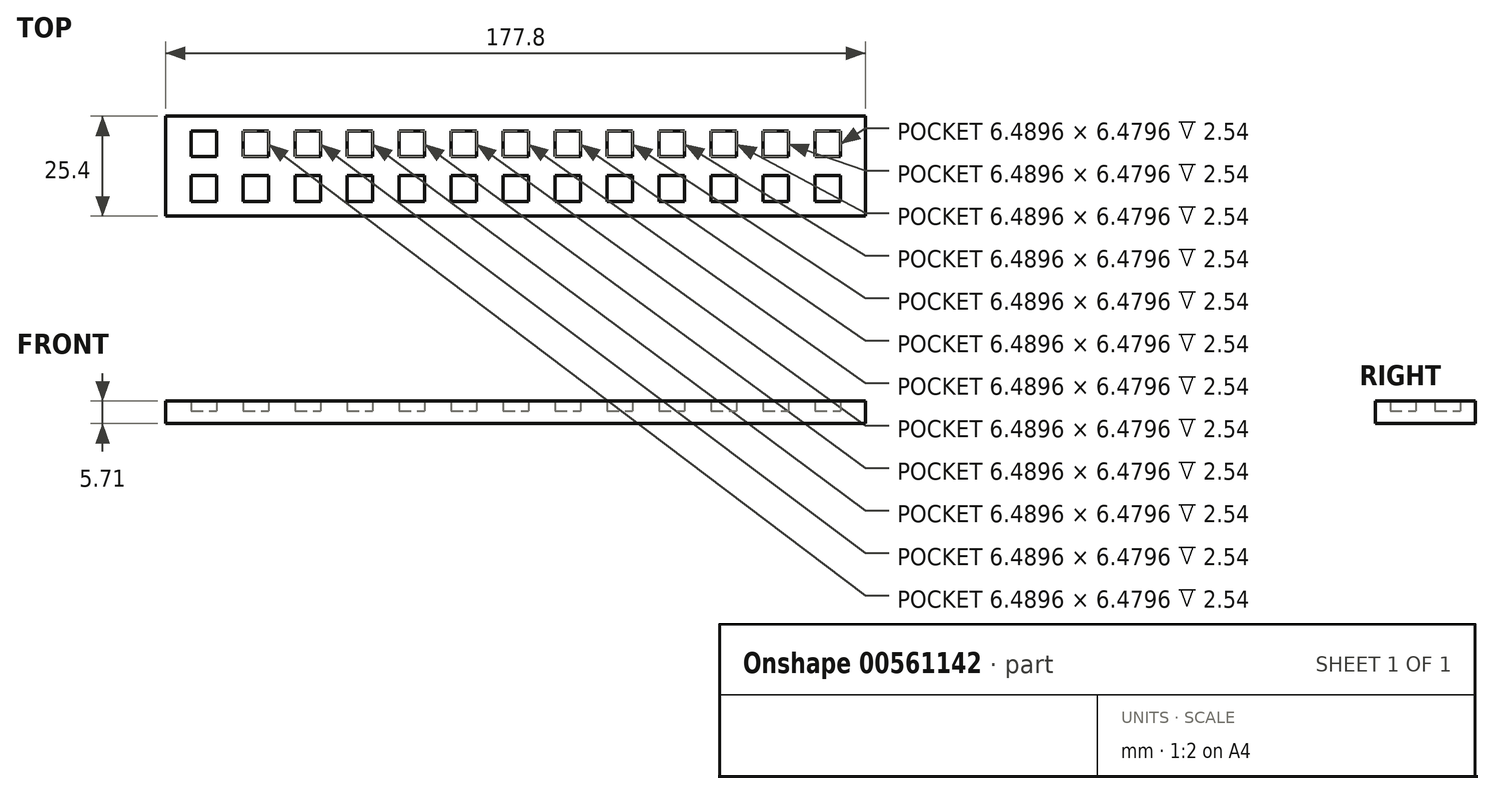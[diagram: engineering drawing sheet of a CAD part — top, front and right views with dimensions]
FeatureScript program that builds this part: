
annotation { "Feature Type Name" : "Feature", "Feature Type Description" : "" }
export const myFeature = defineFeature(function(context is Context, id is Id, definition is map)
    precondition{}
    {
        {
            var Q0;
            Q0=qCreatedBy(makeId("Top.planeOp"),FACE);
            var sketch = newSketch(context, id + "F0", { "sketchPlane" : qUnion([Q0])});
            skLineSegment(sketch, "E0.bottom", {"start": v(0, 0) * mm, "end": v(177.8, 0) * mm});
            skLineSegment(sketch, "E0.top", {"start": v(0, 25.4) * mm, "end": v(177.8, 25.4) * mm});
            skLineSegment(sketch, "E0.left", {"start": v(0, 0) * mm, "end": v(0, 25.4) * mm});
            skLineSegment(sketch, "E0.right", {"start": v(177.8, 0) * mm, "end": v(177.8, 25.4) * mm});
            skSolve(sketch);
        }
        {
            var Q0;
            Q0=makeQuery(id+"F0.imprint","IMPRINT",FACE,{"disambiguationData":[TD([[makeQuery(id+"F0.imprint","IMPRINT",EDGE,{"derivedFrom":sQuery(id+"F0.wireOp",EDGE,"E0.bottom")}),1.0]])]});
            extrude(context, id + "F1", {"entities" : qUnion([Q0]), "depth" : 3.17 * mm, "offsetDistance" : 25.4 * mm});
        }
        {
            var Q0;
            Q0=makeQuery(id+"F1.opExtrude","CAP_FACE",FACE,{"disambiguationData":[OSD([sQuery(id+"F0.wireOp",EDGE,"E0.bottom"),sQuery(id+"F0.wireOp",EDGE,"E0.top"),sQuery(id+"F0.wireOp",EDGE,"E0.left"),sQuery(id+"F0.wireOp",EDGE,"E0.right")])],"isStart":false});
            var sketch = newSketch(context, id + "F2", { "sketchPlane" : qUnion([Q0])});
            skLineSegment(sketch, "E1.right", {"start": v(6.49, 15.11) * mm, "end": v(6.49, 21.6) * mm});
            skLineSegment(sketch, "E2.bottom", {"start": v(6.49, 15.11) * mm, "end": v(12.98, 15.11) * mm});
            skLineSegment(sketch, "E2.top", {"start": v(6.49, 21.6) * mm, "end": v(12.98, 21.6) * mm});
            skLineSegment(sketch, "E2.right", {"start": v(12.98, 15.11) * mm, "end": v(12.98, 21.6) * mm});
            skLineSegment(sketch, "E3.1.0.0", {"start": v(19.7, 21.6) * mm, "end": v(26.19, 21.6) * mm});
            skLineSegment(sketch, "E3.1.0.1", {"start": v(19.7, 15.11) * mm, "end": v(19.7, 21.6) * mm});
            skLineSegment(sketch, "E3.1.0.2", {"start": v(19.7, 15.11) * mm, "end": v(26.19, 15.11) * mm});
            skLineSegment(sketch, "E3.1.0.3", {"start": v(26.19, 15.11) * mm, "end": v(26.19, 21.6) * mm});
            skLineSegment(sketch, "E3.2.0.0", {"start": v(32.9, 21.6) * mm, "end": v(39.4, 21.6) * mm});
            skLineSegment(sketch, "E3.2.0.1", {"start": v(32.9, 15.11) * mm, "end": v(32.9, 21.6) * mm});
            skLineSegment(sketch, "E3.2.0.2", {"start": v(32.9, 15.11) * mm, "end": v(39.4, 15.11) * mm});
            skLineSegment(sketch, "E3.2.0.3", {"start": v(39.4, 15.11) * mm, "end": v(39.4, 21.6) * mm});
            skLineSegment(sketch, "E3.3.0.0", {"start": v(46.11, 21.6) * mm, "end": v(52.6, 21.6) * mm});
            skLineSegment(sketch, "E3.3.0.1", {"start": v(46.11, 15.11) * mm, "end": v(46.11, 21.6) * mm});
            skLineSegment(sketch, "E3.3.0.2", {"start": v(46.11, 15.11) * mm, "end": v(52.6, 15.11) * mm});
            skLineSegment(sketch, "E3.3.0.3", {"start": v(52.6, 15.11) * mm, "end": v(52.6, 21.6) * mm});
            skLineSegment(sketch, "E3.4.0.0", {"start": v(59.32, 21.6) * mm, "end": v(65.81, 21.6) * mm});
            skLineSegment(sketch, "E3.4.0.1", {"start": v(59.32, 15.11) * mm, "end": v(59.32, 21.6) * mm});
            skLineSegment(sketch, "E3.4.0.2", {"start": v(59.32, 15.11) * mm, "end": v(65.81, 15.11) * mm});
            skLineSegment(sketch, "E3.4.0.3", {"start": v(65.81, 15.11) * mm, "end": v(65.81, 21.6) * mm});
            skLineSegment(sketch, "E3.5.0.0", {"start": v(72.53, 21.6) * mm, "end": v(79.02, 21.6) * mm});
            skLineSegment(sketch, "E3.5.0.1", {"start": v(72.53, 15.11) * mm, "end": v(72.53, 21.6) * mm});
            skLineSegment(sketch, "E3.5.0.2", {"start": v(72.53, 15.11) * mm, "end": v(79.02, 15.11) * mm});
            skLineSegment(sketch, "E3.5.0.3", {"start": v(79.02, 15.11) * mm, "end": v(79.02, 21.6) * mm});
            skLineSegment(sketch, "E3.6.0.0", {"start": v(85.74, 21.6) * mm, "end": v(92.23, 21.6) * mm});
            skLineSegment(sketch, "E3.6.0.1", {"start": v(85.74, 15.11) * mm, "end": v(85.74, 21.6) * mm});
            skLineSegment(sketch, "E3.6.0.2", {"start": v(85.74, 15.11) * mm, "end": v(92.23, 15.11) * mm});
            skLineSegment(sketch, "E3.6.0.3", {"start": v(92.23, 15.11) * mm, "end": v(92.23, 21.6) * mm});
            skLineSegment(sketch, "E3.7.0.0", {"start": v(98.95, 21.6) * mm, "end": v(105.44, 21.6) * mm});
            skLineSegment(sketch, "E3.7.0.1", {"start": v(98.95, 15.11) * mm, "end": v(98.95, 21.6) * mm});
            skLineSegment(sketch, "E3.7.0.2", {"start": v(98.95, 15.11) * mm, "end": v(105.44, 15.11) * mm});
            skLineSegment(sketch, "E3.7.0.3", {"start": v(105.44, 15.11) * mm, "end": v(105.44, 21.6) * mm});
            skLineSegment(sketch, "E3.8.0.0", {"start": v(112.15, 21.6) * mm, "end": v(118.64, 21.6) * mm});
            skLineSegment(sketch, "E3.8.0.1", {"start": v(112.15, 15.11) * mm, "end": v(112.15, 21.6) * mm});
            skLineSegment(sketch, "E3.8.0.2", {"start": v(112.15, 15.11) * mm, "end": v(118.64, 15.11) * mm});
            skLineSegment(sketch, "E3.8.0.3", {"start": v(118.64, 15.11) * mm, "end": v(118.64, 21.6) * mm});
            skLineSegment(sketch, "E3.9.0.0", {"start": v(125.36, 21.6) * mm, "end": v(131.85, 21.6) * mm});
            skLineSegment(sketch, "E3.9.0.1", {"start": v(125.36, 15.11) * mm, "end": v(125.36, 21.6) * mm});
            skLineSegment(sketch, "E3.9.0.2", {"start": v(125.36, 15.11) * mm, "end": v(131.85, 15.11) * mm});
            skLineSegment(sketch, "E3.9.0.3", {"start": v(131.85, 15.11) * mm, "end": v(131.85, 21.6) * mm});
            skLineSegment(sketch, "E3.10.0.0", {"start": v(138.57, 21.6) * mm, "end": v(145.06, 21.6) * mm});
            skLineSegment(sketch, "E3.10.0.1", {"start": v(138.57, 15.11) * mm, "end": v(138.57, 21.6) * mm});
            skLineSegment(sketch, "E3.10.0.2", {"start": v(138.57, 15.11) * mm, "end": v(145.06, 15.11) * mm});
            skLineSegment(sketch, "E3.10.0.3", {"start": v(145.06, 15.11) * mm, "end": v(145.06, 21.6) * mm});
            skLineSegment(sketch, "E3.11.0.0", {"start": v(151.78, 21.6) * mm, "end": v(158.27, 21.6) * mm});
            skLineSegment(sketch, "E3.11.0.1", {"start": v(151.78, 15.11) * mm, "end": v(151.78, 21.6) * mm});
            skLineSegment(sketch, "E3.11.0.2", {"start": v(151.78, 15.11) * mm, "end": v(158.27, 15.11) * mm});
            skLineSegment(sketch, "E3.11.0.3", {"start": v(158.27, 15.11) * mm, "end": v(158.27, 21.6) * mm});
            skLineSegment(sketch, "E3.12.0.0", {"start": v(164.99, 21.6) * mm, "end": v(171.48, 21.6) * mm});
            skLineSegment(sketch, "E3.12.0.1", {"start": v(164.99, 15.11) * mm, "end": v(164.99, 21.6) * mm});
            skLineSegment(sketch, "E3.12.0.2", {"start": v(164.99, 15.11) * mm, "end": v(171.48, 15.11) * mm});
            skLineSegment(sketch, "E3.12.0.3", {"start": v(171.48, 15.11) * mm, "end": v(171.48, 21.6) * mm});
            skLineSegment(sketch, "E3.direction1", {"start": v(6.49, 21.6) * mm, "end": v(19.7, 21.6) * mm, "construction": true});
            skLineSegment(sketch, "E4", {"start": v(0, 25.4) * mm, "end": v(177.8, 25.4) * mm});
            skLineSegment(sketch, "E5.right", {"start": v(6.49, 3.8) * mm, "end": v(6.49, 10.27) * mm});
            skLineSegment(sketch, "E6.bottom", {"start": v(6.49, 3.8) * mm, "end": v(12.98, 3.8) * mm});
            skLineSegment(sketch, "E6.top", {"start": v(6.49, 10.27) * mm, "end": v(12.98, 10.27) * mm});
            skLineSegment(sketch, "E6.right", {"start": v(12.98, 3.8) * mm, "end": v(12.98, 10.27) * mm});
            skLineSegment(sketch, "E7.1.0.0", {"start": v(19.7, 10.27) * mm, "end": v(26.19, 10.27) * mm});
            skLineSegment(sketch, "E7.1.0.1", {"start": v(19.7, 3.8) * mm, "end": v(19.7, 10.27) * mm});
            skLineSegment(sketch, "E7.1.0.2", {"start": v(19.7, 3.8) * mm, "end": v(26.19, 3.8) * mm});
            skLineSegment(sketch, "E7.1.0.3", {"start": v(26.19, 3.8) * mm, "end": v(26.19, 10.27) * mm});
            skLineSegment(sketch, "E7.2.0.0", {"start": v(32.9, 10.27) * mm, "end": v(39.4, 10.27) * mm});
            skLineSegment(sketch, "E7.2.0.1", {"start": v(32.9, 3.8) * mm, "end": v(32.9, 10.27) * mm});
            skLineSegment(sketch, "E7.2.0.2", {"start": v(32.9, 3.8) * mm, "end": v(39.4, 3.8) * mm});
            skLineSegment(sketch, "E7.2.0.3", {"start": v(39.4, 3.8) * mm, "end": v(39.4, 10.27) * mm});
            skLineSegment(sketch, "E7.3.0.0", {"start": v(46.11, 10.27) * mm, "end": v(52.6, 10.27) * mm});
            skLineSegment(sketch, "E7.3.0.1", {"start": v(46.11, 3.8) * mm, "end": v(46.11, 10.27) * mm});
            skLineSegment(sketch, "E7.3.0.2", {"start": v(46.11, 3.8) * mm, "end": v(52.6, 3.8) * mm});
            skLineSegment(sketch, "E7.3.0.3", {"start": v(52.6, 3.8) * mm, "end": v(52.6, 10.27) * mm});
            skLineSegment(sketch, "E7.4.0.0", {"start": v(59.32, 10.27) * mm, "end": v(65.81, 10.27) * mm});
            skLineSegment(sketch, "E7.4.0.1", {"start": v(59.32, 3.8) * mm, "end": v(59.32, 10.27) * mm});
            skLineSegment(sketch, "E7.4.0.2", {"start": v(59.32, 3.8) * mm, "end": v(65.81, 3.8) * mm});
            skLineSegment(sketch, "E7.4.0.3", {"start": v(65.81, 3.8) * mm, "end": v(65.81, 10.27) * mm});
            skLineSegment(sketch, "E7.5.0.0", {"start": v(72.53, 10.27) * mm, "end": v(79.02, 10.27) * mm});
            skLineSegment(sketch, "E7.5.0.1", {"start": v(72.53, 3.8) * mm, "end": v(72.53, 10.27) * mm});
            skLineSegment(sketch, "E7.5.0.2", {"start": v(72.53, 3.8) * mm, "end": v(79.02, 3.8) * mm});
            skLineSegment(sketch, "E7.5.0.3", {"start": v(79.02, 3.8) * mm, "end": v(79.02, 10.27) * mm});
            skLineSegment(sketch, "E7.6.0.0", {"start": v(85.74, 10.27) * mm, "end": v(92.23, 10.27) * mm});
            skLineSegment(sketch, "E7.6.0.1", {"start": v(85.74, 3.8) * mm, "end": v(85.74, 10.27) * mm});
            skLineSegment(sketch, "E7.6.0.2", {"start": v(85.74, 3.8) * mm, "end": v(92.23, 3.8) * mm});
            skLineSegment(sketch, "E7.6.0.3", {"start": v(92.23, 3.8) * mm, "end": v(92.23, 10.27) * mm});
            skLineSegment(sketch, "E7.7.0.0", {"start": v(98.95, 10.27) * mm, "end": v(105.44, 10.27) * mm});
            skLineSegment(sketch, "E7.7.0.1", {"start": v(98.95, 3.8) * mm, "end": v(98.95, 10.27) * mm});
            skLineSegment(sketch, "E7.7.0.2", {"start": v(98.95, 3.8) * mm, "end": v(105.44, 3.8) * mm});
            skLineSegment(sketch, "E7.7.0.3", {"start": v(105.44, 3.8) * mm, "end": v(105.44, 10.27) * mm});
            skLineSegment(sketch, "E7.8.0.0", {"start": v(112.15, 10.27) * mm, "end": v(118.64, 10.27) * mm});
            skLineSegment(sketch, "E7.8.0.1", {"start": v(112.15, 3.8) * mm, "end": v(112.15, 10.27) * mm});
            skLineSegment(sketch, "E7.8.0.2", {"start": v(112.15, 3.8) * mm, "end": v(118.64, 3.8) * mm});
            skLineSegment(sketch, "E7.8.0.3", {"start": v(118.64, 3.8) * mm, "end": v(118.64, 10.27) * mm});
            skLineSegment(sketch, "E7.9.0.0", {"start": v(125.36, 10.27) * mm, "end": v(131.85, 10.27) * mm});
            skLineSegment(sketch, "E7.9.0.1", {"start": v(125.36, 3.8) * mm, "end": v(125.36, 10.27) * mm});
            skLineSegment(sketch, "E7.9.0.2", {"start": v(125.36, 3.8) * mm, "end": v(131.85, 3.8) * mm});
            skLineSegment(sketch, "E7.9.0.3", {"start": v(131.85, 3.8) * mm, "end": v(131.85, 10.27) * mm});
            skLineSegment(sketch, "E7.10.0.0", {"start": v(138.57, 10.27) * mm, "end": v(145.06, 10.27) * mm});
            skLineSegment(sketch, "E7.10.0.1", {"start": v(138.57, 3.8) * mm, "end": v(138.57, 10.27) * mm});
            skLineSegment(sketch, "E7.10.0.2", {"start": v(138.57, 3.8) * mm, "end": v(145.06, 3.8) * mm});
            skLineSegment(sketch, "E7.10.0.3", {"start": v(145.06, 3.8) * mm, "end": v(145.06, 10.27) * mm});
            skLineSegment(sketch, "E7.11.0.0", {"start": v(151.78, 10.27) * mm, "end": v(158.27, 10.27) * mm});
            skLineSegment(sketch, "E7.11.0.1", {"start": v(151.78, 3.8) * mm, "end": v(151.78, 10.27) * mm});
            skLineSegment(sketch, "E7.11.0.2", {"start": v(151.78, 3.8) * mm, "end": v(158.27, 3.8) * mm});
            skLineSegment(sketch, "E7.11.0.3", {"start": v(158.27, 3.8) * mm, "end": v(158.27, 10.27) * mm});
            skLineSegment(sketch, "E7.12.0.0", {"start": v(164.99, 10.27) * mm, "end": v(171.48, 10.27) * mm});
            skLineSegment(sketch, "E7.12.0.1", {"start": v(164.99, 3.8) * mm, "end": v(164.99, 10.27) * mm});
            skLineSegment(sketch, "E7.12.0.2", {"start": v(164.99, 3.8) * mm, "end": v(171.48, 3.8) * mm});
            skLineSegment(sketch, "E7.12.0.3", {"start": v(171.48, 3.8) * mm, "end": v(171.48, 10.27) * mm});
            skLineSegment(sketch, "E7.direction1", {"start": v(6.49, 10.27) * mm, "end": v(19.7, 10.27) * mm, "construction": true});
            skSolve(sketch);
        }
        {
            var Q0;
            Q0=makeQuery(id+"F2.imprint","IMPRINT",FACE,{"disambiguationData":[TD([[makeQuery(id+"F2.imprint","IMPRINT",EDGE,{"derivedFrom":sQuery(id+"F2.wireOp",EDGE,"E1.right")}),1.0]])]});
            extrude(context, id + "F3", {"entities" : qUnion([Q0]), "operationType" : NewBodyOperationType.ADD, "depth" : 2.54 * mm, "offsetDistance" : 25.4 * mm});
        }
    });
